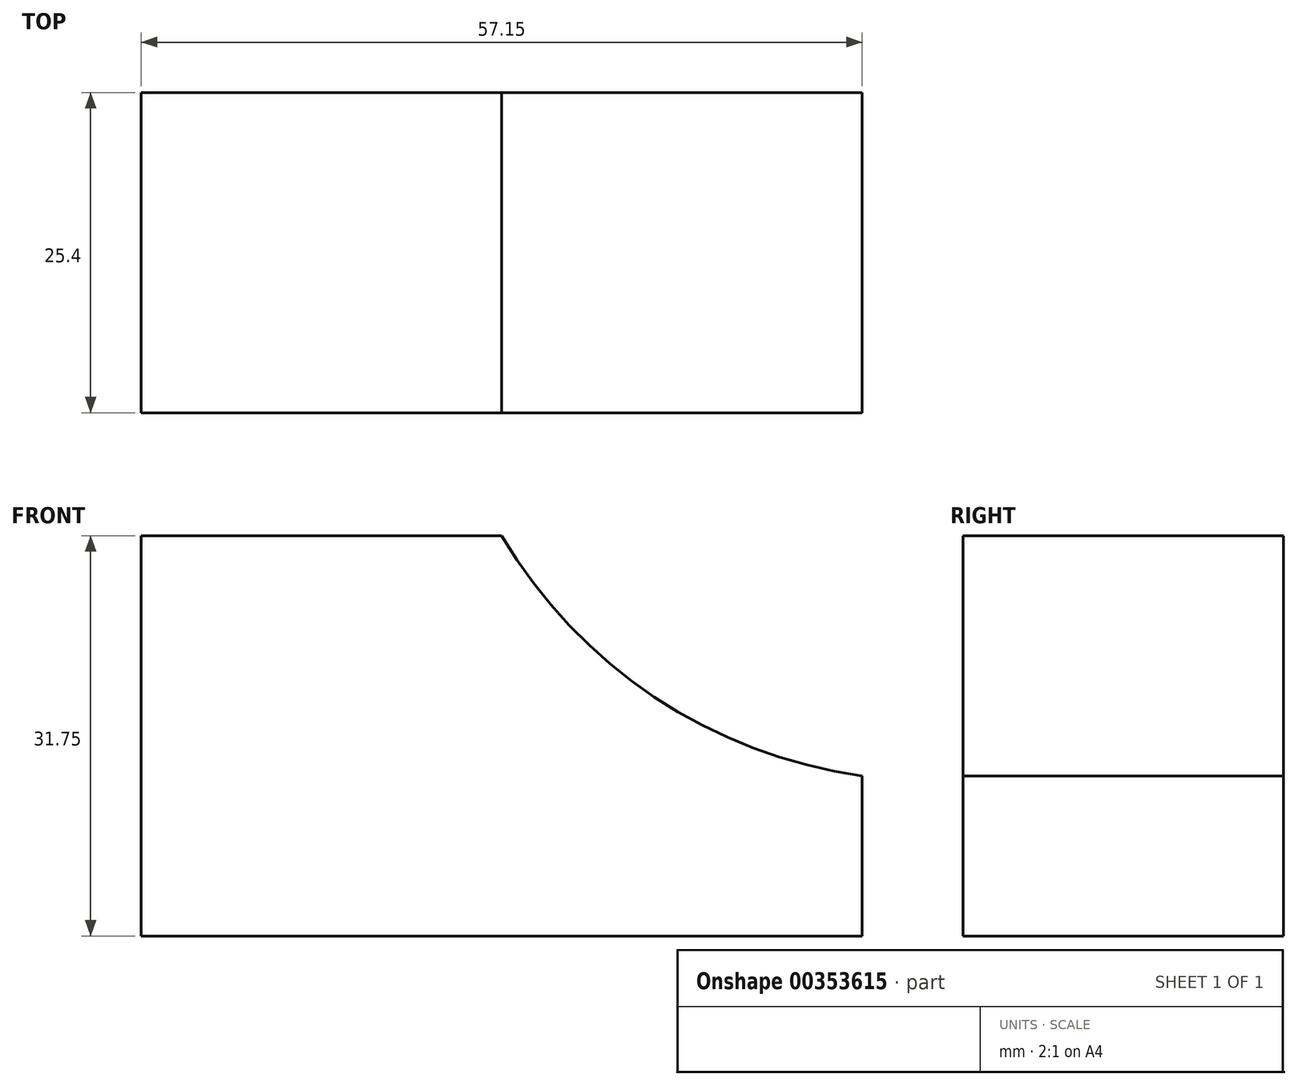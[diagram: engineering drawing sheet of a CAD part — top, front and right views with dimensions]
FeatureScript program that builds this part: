
annotation { "Feature Type Name" : "Feature", "Feature Type Description" : "" }
export const myFeature = defineFeature(function(context is Context, id is Id, definition is map)
    precondition{}
    {
        {
            var Q0;
            Q0=qCreatedBy(makeId("Front.planeOp"),FACE);
            var sketch = newSketch(context, id + "F0", { "sketchPlane" : qUnion([Q0])});
            skLineSegment(sketch, "E0", {"start": v(0, 0) * mm, "end": v(0, 31.75) * mm});
            skLineSegment(sketch, "E1", {"start": v(0, 31.75) * mm, "end": v(57.15, 31.75) * mm});
            skLineSegment(sketch, "E2", {"start": v(57.15, 31.75) * mm, "end": v(57.15, 0) * mm});
            skLineSegment(sketch, "E3", {"start": v(57.15, 0) * mm, "end": v(0, 0) * mm});
            skSolve(sketch);
        }
        {
            var Q0;
            Q0 = qSketchRegion(id + "F0", true);
            extrude(context, id + "F1", {"entities" : qUnion([Q0]), "depth" : 25.4 * mm});
        }
        {
            var Q0;
            Q0=makeQuery(id+"F1.opExtrude","CAP_FACE",FACE,{"disambiguationData":[OSD([sQuery(id+"F0.wireOp",EDGE,"E0"),sQuery(id+"F0.wireOp",EDGE,"E1"),sQuery(id+"F0.wireOp",EDGE,"E2"),sQuery(id+"F0.wireOp",EDGE,"E3")])],"isStart":false});
            var sketch = newSketch(context, id + "F2", { "sketchPlane" : qUnion([Q0])});
            skArc(sketch, "E4", {"start": v(28.57, 31.75) * mm, "mid": v(40.68, 18.95) * mm, "end": v(57.15, 12.7) * mm});
            skLineSegment(sketch, "E5", {"start": v(28.58, 31.75) * mm, "end": v(57.15, 31.75) * mm});
            skLineSegment(sketch, "E6", {"start": v(57.15, 31.75) * mm, "end": v(57.15, 12.7) * mm});
            skSolve(sketch);
        }
        {
            var Q0;
            Q0=makeQuery(id+"F2.imprint","IMPRINT",FACE,{"disambiguationData":[TD([[makeQuery(id+"F2.imprint","IMPRINT",EDGE,{"derivedFrom":sQuery(id+"F2.wireOp",EDGE,"E4")}),1.0]])]});
            extrude(context, id + "F3", {"entities" : qUnion([Q0]), "operationType" : NewBodyOperationType.REMOVE, "oppositeDirection" : true, "depth" : 25.4 * mm});
        }
    });
